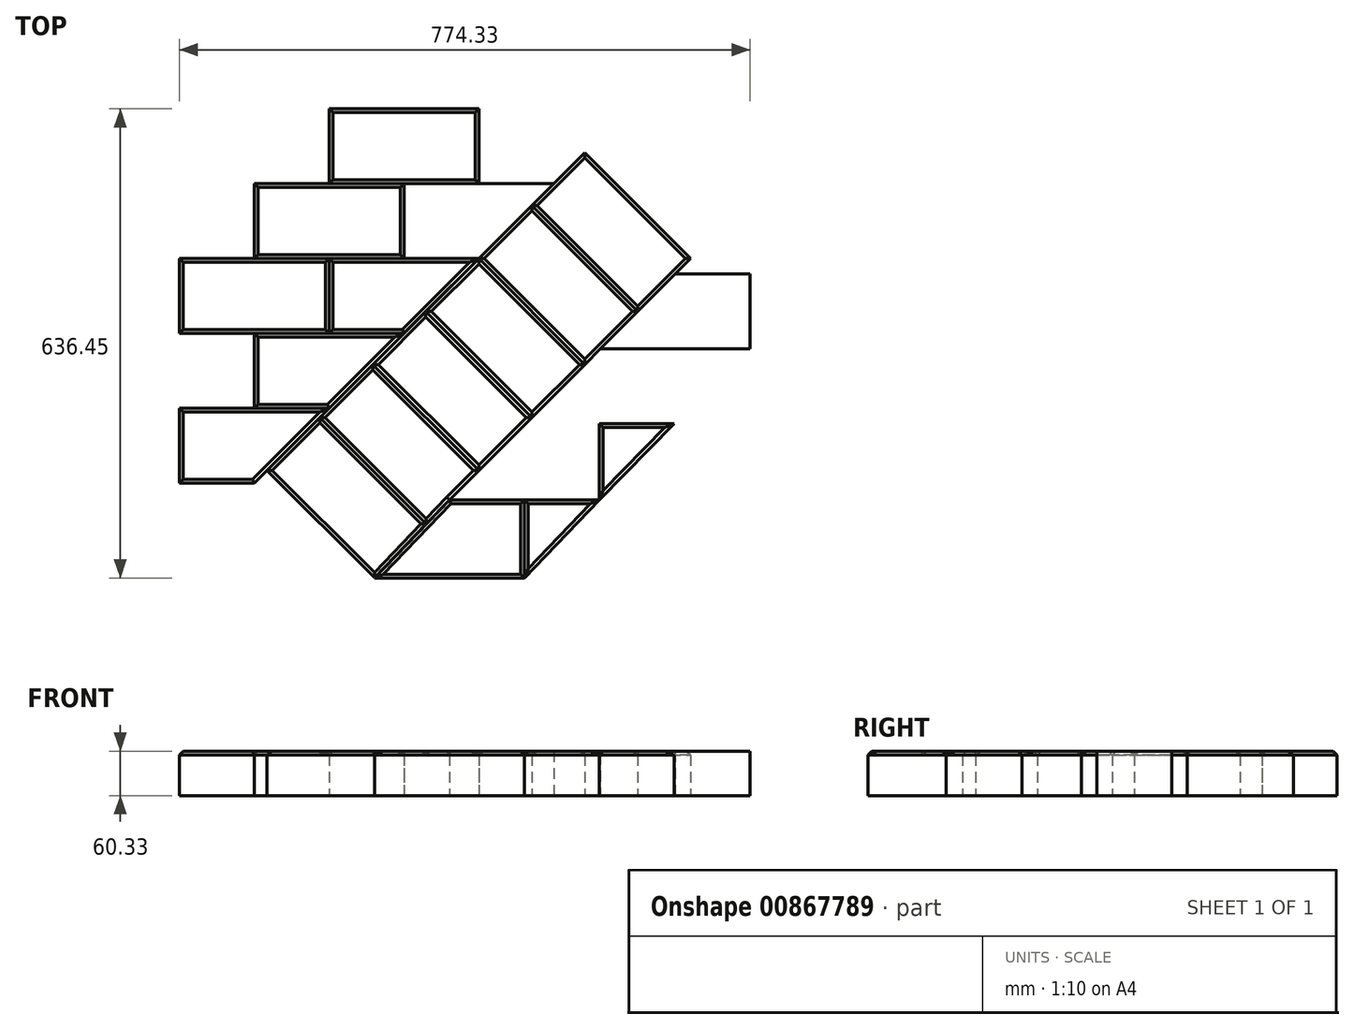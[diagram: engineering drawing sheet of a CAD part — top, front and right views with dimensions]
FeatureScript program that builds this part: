
annotation { "Feature Type Name" : "Feature", "Feature Type Description" : "" }
export const myFeature = defineFeature(function(context is Context, id is Id, definition is map)
    precondition{}
    {
        {
            var Q0;
            Q0=qCreatedBy(makeId("Top.planeOp"),FACE);
            var sketch = newSketch(context, id + "F0", { "sketchPlane" : qUnion([Q0])});
            skLineSegment(sketch, "E0.bottom", {"start": v(1.57, 81.75) * mm, "end": v(103.17, 81.75) * mm});
            skLineSegment(sketch, "E0.top", {"start": v(-100.03, -19.85) * mm, "end": v(103.17, -19.85) * mm});
            skLineSegment(sketch, "E0.right", {"start": v(103.17, 81.75) * mm, "end": v(103.17, -19.85) * mm});
            skLineSegment(sketch, "E1.bottom", {"start": v(103.17, -19.85) * mm, "end": v(0, -19.85) * mm});
            skLineSegment(sketch, "E1.right", {"start": v(0, -19.85) * mm, "end": v(0, -116.67) * mm});
            skLineSegment(sketch, "E2.bottom", {"start": v(0, -19.85) * mm, "end": v(-100.03, -19.85) * mm});
            skLineSegment(sketch, "E2.top", {"start": v(0, -121.45) * mm, "end": v(-201.63, -121.45) * mm});
            skLineSegment(sketch, "E2.left", {"start": v(0, -19.85) * mm, "end": v(0, -121.45) * mm});
            skLineSegment(sketch, "E3.bottom", {"start": v(-6.35, -121.45) * mm, "end": v(-101.6, -121.45) * mm});
            skLineSegment(sketch, "E3.right", {"start": v(-101.6, -121.45) * mm, "end": v(-101.6, -224.62) * mm});
            skLineSegment(sketch, "E4.bottom", {"start": v(-101.6, -121.45) * mm, "end": v(-201.63, -121.45) * mm});
            skLineSegment(sketch, "E4.top", {"start": v(-101.6, -224.62) * mm, "end": v(-304.8, -224.62) * mm});
            skLineSegment(sketch, "E5", {"start": v(-101.6, -224.62) * mm, "end": v(0, -121.45) * mm});
            skLineSegment(sketch, "E6", {"start": v(0, -121.45) * mm, "end": v(103.17, -19.85) * mm});
            skLineSegment(sketch, "E7", {"start": v(-304.8, -224.62) * mm, "end": v(-201.63, -121.45) * mm});
            skPoint(sketch, "E8", {"position": v(-100.03, -19.85) * mm});
            skLineSegment(sketch, "E9", {"start": v(-100.03, -19.85) * mm, "end": v(-201.63, -121.45) * mm});
            skPoint(sketch, "E10.orphan", {"position": v(0, -224.62) * mm});
            skLineSegment(sketch, "E11", {"start": v(-100.03, -19.85) * mm, "end": v(1.57, 81.75) * mm});
            skPoint(sketch, "E12.visualSharp", {"position": v(0, -121.45) * mm});
            skLineSegment(sketch, "E13", {"start": v(-203.2, -224.62) * mm, "end": v(-203.2, -330.46) * mm});
            skLineSegment(sketch, "E14", {"start": v(-203.2, -330.46) * mm, "end": v(-101.6, -224.62) * mm});
            skLineSegment(sketch, "E15", {"start": v(-304.8, -224.62) * mm, "end": v(-406.4, -330.46) * mm});
            skLineSegment(sketch, "E16", {"start": v(-203.2, -330.46) * mm, "end": v(-406.4, -330.46) * mm});
            skLineSegment(sketch, "E17", {"start": v(-49.23, 30.95) * mm, "end": v(-192.92, 174.63) * mm});
            skLineSegment(sketch, "E18", {"start": v(-192.92, 174.63) * mm, "end": v(-264.76, 102.8) * mm});
            skLineSegment(sketch, "E19", {"start": v(-264.76, 102.8) * mm, "end": v(-121.08, -40.9) * mm});
            skLineSegment(sketch, "E20", {"start": v(-264.76, 102.8) * mm, "end": v(-336.6, 30.95) * mm});
            skLineSegment(sketch, "E21", {"start": v(-336.6, 30.95) * mm, "end": v(-192.92, -112.74) * mm});
            skLineSegment(sketch, "E22", {"start": v(-336.6, 30.95) * mm, "end": v(-408.44, -40.9) * mm});
            skLineSegment(sketch, "E23", {"start": v(-408.44, -40.9) * mm, "end": v(-264.76, -184.58) * mm});
            skLineSegment(sketch, "E24", {"start": v(-408.44, -40.9) * mm, "end": v(-480.29, -112.74) * mm});
            skLineSegment(sketch, "E25", {"start": v(-480.29, -112.74) * mm, "end": v(-335.95, -257.07) * mm});
            skLineSegment(sketch, "E26", {"start": v(-480.29, -112.74) * mm, "end": v(-552.13, -184.58) * mm});
            skLineSegment(sketch, "E27", {"start": v(-552.13, -184.58) * mm, "end": v(-406.33, -330.38) * mm});
            skLineSegment(sketch, "E28", {"start": v(-192.92, 174.63) * mm, "end": v(-121.08, 246.47) * mm});
            skLineSegment(sketch, "E29", {"start": v(-121.08, 246.47) * mm, "end": v(22.6, 102.8) * mm});
            skLineSegment(sketch, "E30", {"start": v(22.6, 102.8) * mm, "end": v(1.57, 81.75) * mm});
            skLineSegment(sketch, "E31", {"start": v(-264.76, 102.8) * mm, "end": v(-467.96, 102.8) * mm});
            skLineSegment(sketch, "E32", {"start": v(-467.96, 102.8) * mm, "end": v(-467.96, 1.2) * mm});
            skLineSegment(sketch, "E33", {"start": v(-467.96, 1.2) * mm, "end": v(-366.36, 1.2) * mm});
            skLineSegment(sketch, "E34", {"start": v(-467.96, 1.2) * mm, "end": v(-569.56, 1.2) * mm});
            skLineSegment(sketch, "E35", {"start": v(-569.56, 1.2) * mm, "end": v(-569.56, -100.4) * mm});
            skLineSegment(sketch, "E36", {"start": v(-569.56, -100.4) * mm, "end": v(-467.96, -100.4) * mm});
            skLineSegment(sketch, "E37", {"start": v(-366.36, 102.8) * mm, "end": v(-366.36, 204.4) * mm});
            skLineSegment(sketch, "E38", {"start": v(-366.36, 204.4) * mm, "end": v(-569.56, 204.4) * mm});
            skLineSegment(sketch, "E39", {"start": v(-569.56, 204.4) * mm, "end": v(-569.56, 102.8) * mm});
            skLineSegment(sketch, "E40", {"start": v(-569.56, 102.8) * mm, "end": v(-366.36, 102.8) * mm});
            skLineSegment(sketch, "E41", {"start": v(-366.36, 204.4) * mm, "end": v(-163.16, 204.4) * mm});
            skPoint(sketch, "E42.oppositeSnap0", {"position": v(-518.76, 1.2) * mm});
            skLineSegment(sketch, "E42.bottom", {"start": v(-467.96, 102.8) * mm, "end": v(-671.16, 102.8) * mm});
            skLineSegment(sketch, "E42.top", {"start": v(-467.96, 1.2) * mm, "end": v(-671.16, 1.2) * mm});
            skLineSegment(sketch, "E42.right", {"start": v(-671.16, 102.8) * mm, "end": v(-671.16, 1.2) * mm});
            skLineSegment(sketch, "E43.bottom", {"start": v(-569.56, 1.2) * mm, "end": v(-772.76, 1.2) * mm});
            skLineSegment(sketch, "E43.top", {"start": v(-569.56, -100.4) * mm, "end": v(-772.76, -100.4) * mm});
            skLineSegment(sketch, "E43.right", {"start": v(-772.76, 1.2) * mm, "end": v(-772.76, -100.4) * mm});
            skLineSegment(sketch, "E44", {"start": v(-671.16, -100.4) * mm, "end": v(-671.16, -202) * mm});
            skLineSegment(sketch, "E45", {"start": v(-552.13, -184.58) * mm, "end": v(-569.56, -202) * mm});
            skLineSegment(sketch, "E46", {"start": v(-569.56, -202) * mm, "end": v(-671.16, -202) * mm});
            skLineSegment(sketch, "E47", {"start": v(-552.13, -184.58) * mm, "end": v(-623.97, -256.42) * mm});
            skLineSegment(sketch, "E48", {"start": v(-623.97, -256.42) * mm, "end": v(-478.17, -402.22) * mm});
            skLineSegment(sketch, "E49", {"start": v(-478.17, -402.22) * mm, "end": v(-406.33, -330.38) * mm});
            skLineSegment(sketch, "E50.bottom", {"start": v(-467.96, 204.4) * mm, "end": v(-264.76, 204.4) * mm});
            skLineSegment(sketch, "E50.top", {"start": v(-467.96, 306) * mm, "end": v(-264.76, 306) * mm});
            skLineSegment(sketch, "E50.left", {"start": v(-467.96, 204.4) * mm, "end": v(-467.96, 306) * mm});
            skLineSegment(sketch, "E50.right", {"start": v(-264.76, 204.4) * mm, "end": v(-264.76, 306) * mm});
            skLineSegment(sketch, "E51", {"start": v(-121.08, 246.47) * mm, "end": v(22.6, 390.16) * mm});
            skLineSegment(sketch, "E52", {"start": v(22.6, 390.16) * mm, "end": v(-49.23, 462) * mm});
            skLineSegment(sketch, "E53", {"start": v(-49.23, 462) * mm, "end": v(-192.92, 318.32) * mm});
            skLineSegment(sketch, "E54", {"start": v(-192.92, 318.32) * mm, "end": v(-121.08, 246.47) * mm});
            skLineSegment(sketch, "E55", {"start": v(22.6, 102.8) * mm, "end": v(94.45, 174.63) * mm});
            skLineSegment(sketch, "E56", {"start": v(22.6, 390.16) * mm, "end": v(94.45, 318.32) * mm});
            skLineSegment(sketch, "E57", {"start": v(-121.08, 246.47) * mm, "end": v(22.6, 246.47) * mm});
            skLineSegment(sketch, "E58", {"start": v(94.45, 318.32) * mm, "end": v(22.6, 246.47) * mm});
            skLineSegment(sketch, "E59", {"start": v(94.45, 174.63) * mm, "end": v(22.6, 246.47) * mm});
            skLineSegment(sketch, "E60", {"start": v(94.45, 318.32) * mm, "end": v(166.3, 246.47) * mm});
            skLineSegment(sketch, "E61", {"start": v(166.3, 246.47) * mm, "end": v(94.45, 174.63) * mm});
            skLineSegment(sketch, "E62", {"start": v(-49.23, 462) * mm, "end": v(-121.08, 533.84) * mm});
            skLineSegment(sketch, "E63", {"start": v(-121.08, 533.84) * mm, "end": v(-264.76, 390.16) * mm});
            skLineSegment(sketch, "E64", {"start": v(-264.76, 390.16) * mm, "end": v(-192.92, 318.32) * mm});
            skLineSegment(sketch, "E65", {"start": v(-264.76, 390.16) * mm, "end": v(-336.6, 462) * mm});
            skLineSegment(sketch, "E66", {"start": v(-336.6, 462) * mm, "end": v(-192.92, 605.68) * mm});
            skLineSegment(sketch, "E67", {"start": v(-192.92, 605.68) * mm, "end": v(-121.08, 533.84) * mm});
            skLineSegment(sketch, "E68", {"start": v(-264.76, 306) * mm, "end": v(-180.6, 306) * mm});
            skLineSegment(sketch, "E69", {"start": v(-366.36, 306) * mm, "end": v(-366.36, 407.6) * mm});
            skLineSegment(sketch, "E70", {"start": v(-366.36, 407.6) * mm, "end": v(-282.2, 407.6) * mm});
            skLineSegment(sketch, "E71", {"start": v(103.17, -19.85) * mm, "end": v(309.5, 183.35) * mm});
            skLineSegment(sketch, "E72", {"start": v(1.57, 81.75) * mm, "end": v(206.33, 81.75) * mm});
            skLineSegment(sketch, "E73", {"start": v(206.33, 81.75) * mm, "end": v(206.33, 183.35) * mm});
            skLineSegment(sketch, "E74", {"start": v(206.33, 183.35) * mm, "end": v(103.17, 183.35) * mm});
            skLineSegment(sketch, "E75", {"start": v(206.33, 183.35) * mm, "end": v(309.5, 183.35) * mm});
            skLineSegment(sketch, "E76", {"start": v(309.5, 183.35) * mm, "end": v(309.5, 284.95) * mm});
            skLineSegment(sketch, "E77", {"start": v(309.5, 284.95) * mm, "end": v(127.82, 284.95) * mm});
            skLineSegment(sketch, "E78", {"start": v(309.5, 284.95) * mm, "end": v(360.28, 235.41) * mm});
            skLineSegment(sketch, "E79", {"start": v(309.5, 183.35) * mm, "end": v(360.28, 235.41) * mm});
            skLineSegment(sketch, "E80", {"start": v(309.5, 284.95) * mm, "end": v(99.72, 494.73) * mm});
            skLineSegment(sketch, "E81", {"start": v(229.63, 284.95) * mm, "end": v(215.12, 379.33) * mm});
            skLineSegment(sketch, "E82", {"start": v(215.12, 379.33) * mm, "end": v(33.44, 379.33) * mm});
            skLineSegment(sketch, "E83", {"start": v(33.44, 379.33) * mm, "end": v(-36.18, 448.94) * mm});
            skLineSegment(sketch, "E84", {"start": v(-36.18, 448.94) * mm, "end": v(145.5, 448.94) * mm});
            skLineSegment(sketch, "E85", {"start": v(145.5, 379.33) * mm, "end": v(145.5, 448.94) * mm});
            skSolve(sketch);
        }
        {
            var Q0;
            {var subQ0=sQuery(id+"F0.wireOp",EDGE,"E25");Q0=makeQuery(id+"F0.imprint","IMPRINT",FACE,{"disambiguationData":[TD([[makeQuery(id+"F0.imprint","IMPRINT",EDGE,{"derivedFrom":subQ0}),-1.0]])]});}
            extrude(context, id + "F1", {"entities" : qUnion([Q0]), "depth" : 60.32 * mm, "offsetDistance" : 25.4 * mm});
        }
        {
            var Q0;
            Q0=makeQuery(id+"F1.opExtrude","CAP_EDGE",EDGE,{"disambiguationData":[OSD([sQuery(id+"F0.wireOp",EDGE,"E15")])],"isStart":false});
            var Q1;
            Q1=makeQuery(id+"F1.opExtrude","CAP_EDGE",EDGE,{"disambiguationData":[OSD([sQuery(id+"F0.wireOp",EDGE,"E27")])],"isStart":false});
            var Q2;
            Q2=makeQuery(id+"F1.opExtrude","CAP_EDGE",EDGE,{"disambiguationData":[OSD([sQuery(id+"F0.wireOp",EDGE,"E26")])],"isStart":false});
            var Q3;
            Q3=makeQuery(id+"F1.opExtrude","CAP_EDGE",EDGE,{"disambiguationData":[OSD([sQuery(id+"F0.wireOp",EDGE,"E25")])],"isStart":false});
            chamfer(context, id + "F2", {"entities" : qUnion([Q0, Q1, Q2, Q3]), "width" : 5.08 * mm, "tangentPropagation" : true});
        }
        {
            var Q0;
            {var subQ4=sQuery(id+"F0.wireOp",EDGE,"E23");Q0=makeQuery(id+"F0.imprint","IMPRINT",FACE,{"disambiguationData":[TD([[makeQuery(id+"F0.imprint","IMPRINT",EDGE,{"derivedFrom":subQ4}),-1.0]])]});}
            extrude(context, id + "F3", {"entities" : qUnion([Q0]), "operationType" : NewBodyOperationType.ADD, "depth" : 60.32 * mm, "offsetDistance" : 25.4 * mm});
        }
        {
            var Q0;
            Q0=makeQuery(id+"F3.opExtrude","CAP_FACE",FACE,{"disambiguationData":[OSD([sQuery(id+"F0.wireOp",EDGE,"E7"),sQuery(id+"F0.wireOp",EDGE,"E15"),sQuery(id+"F0.wireOp",EDGE,"E23"),sQuery(id+"F0.wireOp",EDGE,"E24"),sQuery(id+"F0.wireOp",EDGE,"E25")])],"isStart":false});
            chamfer(context, id + "F4", {"entities" : qUnion([Q0]), "width" : 5.08 * mm, "tangentPropagation" : true});
        }
        {
            var Q0;
            {var subQ0=sQuery(id+"F0.wireOp",EDGE,"E21");Q0=makeQuery(id+"F0.imprint","IMPRINT",FACE,{"disambiguationData":[TD([[makeQuery(id+"F0.imprint","IMPRINT",EDGE,{"derivedFrom":subQ0}),-1.0]])]});}
            extrude(context, id + "F5", {"entities" : qUnion([Q0]), "operationType" : NewBodyOperationType.ADD, "depth" : 60.32 * mm, "offsetDistance" : 25.4 * mm});
        }
        {
            var Q0;
            Q0=makeQuery(id+"F5.opExtrude","CAP_FACE",FACE,{"disambiguationData":[OSD([sQuery(id+"F0.wireOp",EDGE,"E7"),sQuery(id+"F0.wireOp",EDGE,"E9"),sQuery(id+"F0.wireOp",EDGE,"E21"),sQuery(id+"F0.wireOp",EDGE,"E22"),sQuery(id+"F0.wireOp",EDGE,"E23")])],"isStart":false});
            chamfer(context, id + "F6", {"entities" : qUnion([Q0]), "width" : 5.08 * mm, "tangentPropagation" : true});
        }
        {
            var Q0;
            {var subQ0=sQuery(id+"F0.wireOp",EDGE,"E19");Q0=makeQuery(id+"F0.imprint","IMPRINT",FACE,{"disambiguationData":[TD([[makeQuery(id+"F0.imprint","IMPRINT",EDGE,{"derivedFrom":subQ0}),-1.0]])]});}
            var Q1;
            {var subQ0=sQuery(id+"F0.wireOp",EDGE,"E17");Q1=makeQuery(id+"F0.imprint","IMPRINT",FACE,{"disambiguationData":[TD([[makeQuery(id+"F0.imprint","IMPRINT",EDGE,{"derivedFrom":subQ0}),-1.0]])]});}
            var Q2;
            {var subQ0=sQuery(id+"F0.wireOp",EDGE,"E1.bottom");Q2=makeQuery(id+"F0.imprint","IMPRINT",FACE,{"disambiguationData":[TD([[makeQuery(id+"F0.imprint","IMPRINT",EDGE,{"derivedFrom":subQ0}),1.0]])]});}
            var Q3;
            Q3=makeQuery(id+"F0.imprint","IMPRINT",FACE,{"disambiguationData":[TD([[makeQuery(id+"F0.imprint","IMPRINT",EDGE,{"derivedFrom":sQuery(id+"F0.wireOp",EDGE,"E2.top")}),1.0]])]});
            var Q4;
            {var subQ2=sQuery(id+"F0.wireOp",EDGE,"E13");Q4=makeQuery(id+"F0.imprint","IMPRINT",FACE,{"disambiguationData":[TD([[makeQuery(id+"F0.imprint","IMPRINT",EDGE,{"derivedFrom":subQ2}),1.0]])]});}
            extrude(context, id + "F7", {"entities" : qUnion([Q0, Q1, Q2, Q3, Q4]), "operationType" : NewBodyOperationType.ADD, "depth" : 60.32 * mm, "offsetDistance" : 25.4 * mm});
        }
        {
            var Q0;
            Q0=makeQuery(id+"F7.opExtrude","CAP_FACE",FACE,{"disambiguationData":[OSD([sQuery(id+"F0.wireOp",EDGE,"E4.top"),sQuery(id+"F0.wireOp",EDGE,"E13"),sQuery(id+"F0.wireOp",EDGE,"E14")])],"isStart":false});
            var Q1;
            Q1=makeQuery(id+"F7.opExtrude","CAP_FACE",FACE,{"disambiguationData":[OSD([sQuery(id+"F0.wireOp",EDGE,"E2.top"),sQuery(id+"F0.wireOp",EDGE,"E3.bottom"),sQuery(id+"F0.wireOp",EDGE,"E3.right"),sQuery(id+"F0.wireOp",EDGE,"E5")])],"isStart":false});
            var Q2;
            Q2=makeQuery(id+"F7.opExtrude","CAP_FACE",FACE,{"disambiguationData":[OSD([sQuery(id+"F0.wireOp",EDGE,"E1.bottom"),sQuery(id+"F0.wireOp",EDGE,"E6"),sQuery(id+"F0.wireOp",EDGE,"E2.left")])],"isStart":false});
            var Q3;
            Q3=makeQuery(id+"F7.opExtrude","CAP_FACE",FACE,{"disambiguationData":[OSD([sQuery(id+"F0.wireOp",EDGE,"E11"),sQuery(id+"F0.wireOp",EDGE,"E17"),sQuery(id+"F0.wireOp",EDGE,"E28"),sQuery(id+"F0.wireOp",EDGE,"E29"),sQuery(id+"F0.wireOp",EDGE,"E30")])],"isStart":false});
            var Q4;
            Q4=makeQuery(id+"F7.opExtrude","CAP_FACE",FACE,{"disambiguationData":[OSD([sQuery(id+"F0.wireOp",EDGE,"E9"),sQuery(id+"F0.wireOp",EDGE,"E19"),sQuery(id+"F0.wireOp",EDGE,"E20"),sQuery(id+"F0.wireOp",EDGE,"E21")])],"isStart":false});
            chamfer(context, id + "F8", {"entities" : qUnion([Q0, Q1, Q2, Q3, Q4]), "width" : 5.08 * mm, "tangentPropagation" : true});
        }
        {
            var Q0;
            {var subQ3=sQuery(id+"F0.wireOp",EDGE,"E13");Q0=makeQuery(id+"F0.imprint","IMPRINT",FACE,{"disambiguationData":[TD([[makeQuery(id+"F0.imprint","IMPRINT",EDGE,{"derivedFrom":subQ3}),-1.0]])]});}
            var Q1;
            {var subQ5=sQuery(id+"F0.wireOp",EDGE,"E2.bottom");Q1=makeQuery(id+"F0.imprint","IMPRINT",FACE,{"disambiguationData":[TD([[makeQuery(id+"F0.imprint","IMPRINT",EDGE,{"derivedFrom":subQ5}),1.0]])]});}
            extrude(context, id + "F9", {"entities" : qUnion([Q0, Q1]), "depth" : 60.32 * mm, "offsetDistance" : 25.4 * mm});
        }
        {
            var Q0;
            Q0=makeQuery(id+"F9.opExtrude","CAP_FACE",FACE,{"disambiguationData":[OSD([sQuery(id+"F0.wireOp",EDGE,"E4.top"),sQuery(id+"F0.wireOp",EDGE,"E13"),sQuery(id+"F0.wireOp",EDGE,"E15"),sQuery(id+"F0.wireOp",EDGE,"E16")])],"isStart":false});
            var Q1;
            Q1=makeQuery(id+"F9.opExtrude","CAP_FACE",FACE,{"disambiguationData":[OSD([sQuery(id+"F0.wireOp",EDGE,"E2.bottom"),sQuery(id+"F0.wireOp",EDGE,"E2.top"),sQuery(id+"F0.wireOp",EDGE,"E3.bottom"),sQuery(id+"F0.wireOp",EDGE,"E4.bottom"),sQuery(id+"F0.wireOp",EDGE,"E9"),sQuery(id+"F0.wireOp",EDGE,"E2.left")])],"isStart":false});
            chamfer(context, id + "F10", {"entities" : qUnion([Q0, Q1]), "width" : 5.08 * mm, "tangentPropagation" : true});
        }
        {
            var Q0;
            {var subQ3=sQuery(id+"F0.wireOp",EDGE,"E17");Q0=makeQuery(id+"F0.imprint","IMPRINT",FACE,{"disambiguationData":[TD([[makeQuery(id+"F0.imprint","IMPRINT",EDGE,{"derivedFrom":subQ3}),1.0]])]});}
            var Q1;
            {var subQ5=sQuery(id+"F0.wireOp",EDGE,"E4.bottom");Q1=makeQuery(id+"F0.imprint","IMPRINT",FACE,{"disambiguationData":[TD([[makeQuery(id+"F0.imprint","IMPRINT",EDGE,{"derivedFrom":subQ5}),1.0]])]});}
            extrude(context, id + "F11", {"entities" : qUnion([Q0, Q1]), "depth" : 60.32 * mm, "offsetDistance" : 25.4 * mm});
        }
        {
            var Q0;
            Q0=makeQuery(id+"F11.opExtrude","CAP_FACE",FACE,{"disambiguationData":[OSD([sQuery(id+"F0.wireOp",EDGE,"E4.bottom"),sQuery(id+"F0.wireOp",EDGE,"E4.top"),sQuery(id+"F0.wireOp",EDGE,"E3.right"),sQuery(id+"F0.wireOp",EDGE,"E7")])],"isStart":false});
            var Q1;
            Q1=makeQuery(id+"F11.opExtrude","CAP_FACE",FACE,{"disambiguationData":[OSD([sQuery(id+"F0.wireOp",EDGE,"E9"),sQuery(id+"F0.wireOp",EDGE,"E11"),sQuery(id+"F0.wireOp",EDGE,"E17"),sQuery(id+"F0.wireOp",EDGE,"E18"),sQuery(id+"F0.wireOp",EDGE,"E19")])],"isStart":false});
            chamfer(context, id + "F12", {"entities" : qUnion([Q0, Q1]), "width" : 5.08 * mm, "tangentPropagation" : true});
        }
        {
            var Q0;
            {var subQ1=sQuery(id+"F0.wireOp",EDGE,"E0.bottom");Q0=makeQuery(id+"F0.imprint","IMPRINT",FACE,{"disambiguationData":[TD([[makeQuery(id+"F0.imprint","IMPRINT",EDGE,{"derivedFrom":subQ1}),-1.0]])]});}
            extrude(context, id + "F13", {"entities" : qUnion([Q0]), "depth" : 60.32 * mm, "offsetDistance" : 25.4 * mm});
        }
        {
            var Q0;
            Q0=makeQuery(id+"F0.imprint","IMPRINT",FACE,{"disambiguationData":[TD([[makeQuery(id+"F0.imprint","IMPRINT",EDGE,{"derivedFrom":sQuery(id+"F0.wireOp",EDGE,"E50.top")}),-1.0]])]});
            var Q1;
            {var subQ1=sQuery(id+"F0.wireOp",EDGE,"E42.top");Q1=makeQuery(id+"F0.imprint","IMPRINT",FACE,{"disambiguationData":[TD([[makeQuery(id+"F0.imprint","IMPRINT",EDGE,{"derivedFrom":subQ1}),-1.0]])]});}
            var Q2;
            {var subQ3=sQuery(id+"F0.wireOp",EDGE,"E26");Q2=makeQuery(id+"F0.imprint","IMPRINT",FACE,{"disambiguationData":[TD([[makeQuery(id+"F0.imprint","IMPRINT",EDGE,{"derivedFrom":subQ3}),-1.0]])]});}
            extrude(context, id + "F14", {"entities" : qUnion([Q0, Q1, Q2]), "operationType" : NewBodyOperationType.ADD, "depth" : 60.32 * mm, "offsetDistance" : 25.4 * mm});
        }
        {
            var Q0;
            Q0=makeQuery(id+"F14.opExtrude","CAP_FACE",FACE,{"disambiguationData":[OSD([sQuery(id+"F0.wireOp",EDGE,"E50.bottom"),sQuery(id+"F0.wireOp",EDGE,"E50.top"),sQuery(id+"F0.wireOp",EDGE,"E50.left"),sQuery(id+"F0.wireOp",EDGE,"E50.right")])],"isStart":false});
            var Q1;
            Q1=makeQuery(id+"F14.opExtrude","CAP_FACE",FACE,{"disambiguationData":[OSD([sQuery(id+"F0.wireOp",EDGE,"E42.bottom"),sQuery(id+"F0.wireOp",EDGE,"E42.top"),sQuery(id+"F0.wireOp",EDGE,"E32"),sQuery(id+"F0.wireOp",EDGE,"E42.right"),sQuery(id+"F0.wireOp",EDGE,"E43.bottom")])],"isStart":false});
            var Q2;
            Q2=makeQuery(id+"F14.opExtrude","CAP_FACE",FACE,{"disambiguationData":[OSD([sQuery(id+"F0.wireOp",EDGE,"E24"),sQuery(id+"F0.wireOp",EDGE,"E26"),sQuery(id+"F0.wireOp",EDGE,"E36"),sQuery(id+"F0.wireOp",EDGE,"E43.top"),sQuery(id+"F0.wireOp",EDGE,"E44"),sQuery(id+"F0.wireOp",EDGE,"E46"),sQuery(id+"F0.wireOp",EDGE,"E47")])],"isStart":false});
            chamfer(context, id + "F15", {"entities" : qUnion([Q0, Q1, Q2]), "width" : 5.08 * mm, "tangentPropagation" : true});
        }
        {
            var Q0;
            {var subQ3=sQuery(id+"F0.wireOp",EDGE,"E37");Q0=makeQuery(id+"F0.imprint","IMPRINT",FACE,{"disambiguationData":[TD([[makeQuery(id+"F0.imprint","IMPRINT",EDGE,{"derivedFrom":subQ3}),1.0]])]});}
            var Q1;
            {var subQ4=sQuery(id+"F0.wireOp",EDGE,"E33");Q1=makeQuery(id+"F0.imprint","IMPRINT",FACE,{"disambiguationData":[TD([[makeQuery(id+"F0.imprint","IMPRINT",EDGE,{"derivedFrom":subQ4}),-1.0]])]});}
            extrude(context, id + "F16", {"entities" : qUnion([Q0, Q1]), "depth" : 60.32 * mm, "offsetDistance" : 25.4 * mm});
        }
        {
            var Q0;
            Q0=makeQuery(id+"F16.opExtrude","CAP_FACE",FACE,{"disambiguationData":[OSD([sQuery(id+"F0.wireOp",EDGE,"E37"),sQuery(id+"F0.wireOp",EDGE,"E38"),sQuery(id+"F0.wireOp",EDGE,"E39"),sQuery(id+"F0.wireOp",EDGE,"E40"),sQuery(id+"F0.wireOp",EDGE,"E42.bottom"),sQuery(id+"F0.wireOp",EDGE,"E50.bottom")])],"isStart":false});
            var Q1;
            Q1=makeQuery(id+"F16.opExtrude","CAP_FACE",FACE,{"disambiguationData":[OSD([sQuery(id+"F0.wireOp",EDGE,"E22"),sQuery(id+"F0.wireOp",EDGE,"E24"),sQuery(id+"F0.wireOp",EDGE,"E33"),sQuery(id+"F0.wireOp",EDGE,"E36"),sQuery(id+"F0.wireOp",EDGE,"E42.top"),sQuery(id+"F0.wireOp",EDGE,"E35")])],"isStart":false});
            chamfer(context, id + "F17", {"entities" : qUnion([Q0, Q1]), "width" : 5.08 * mm, "tangentPropagation" : true});
        }
        {
            var Q0;
            {var subQ2=sQuery(id+"F0.wireOp",EDGE,"E18");Q0=makeQuery(id+"F0.imprint","IMPRINT",FACE,{"disambiguationData":[TD([[makeQuery(id+"F0.imprint","IMPRINT",EDGE,{"derivedFrom":subQ2}),-1.0]])]});}
            var Q1;
            {var subQ3=sQuery(id+"F0.wireOp",EDGE,"E35");Q1=makeQuery(id+"F0.imprint","IMPRINT",FACE,{"disambiguationData":[TD([[makeQuery(id+"F0.imprint","IMPRINT",EDGE,{"derivedFrom":subQ3}),-1.0]])]});}
            extrude(context, id + "F18", {"entities" : qUnion([Q0, Q1]), "depth" : 60.32 * mm, "offsetDistance" : 25.4 * mm});
        }
        {
            var Q0;
            {var subQ1=sQuery(id+"F0.wireOp",EDGE,"E20");Q0=makeQuery(id+"F0.imprint","IMPRINT",FACE,{"disambiguationData":[TD([[makeQuery(id+"F0.imprint","IMPRINT",EDGE,{"derivedFrom":subQ1}),-1.0]])]});}
            extrude(context, id + "F19", {"entities" : qUnion([Q0]), "depth" : 60.32 * mm, "offsetDistance" : 25.4 * mm});
        }
        {
            var Q0;
            Q0=makeQuery(id+"F19.opExtrude","CAP_FACE",FACE,{"disambiguationData":[OSD([sQuery(id+"F0.wireOp",EDGE,"E20"),sQuery(id+"F0.wireOp",EDGE,"E22"),sQuery(id+"F0.wireOp",EDGE,"E31"),sQuery(id+"F0.wireOp",EDGE,"E33"),sQuery(id+"F0.wireOp",EDGE,"E40"),sQuery(id+"F0.wireOp",EDGE,"E32")])],"isStart":false});
            chamfer(context, id + "F20", {"entities" : qUnion([Q0]), "width" : 5.08 * mm, "tangentPropagation" : true});
        }
    });
